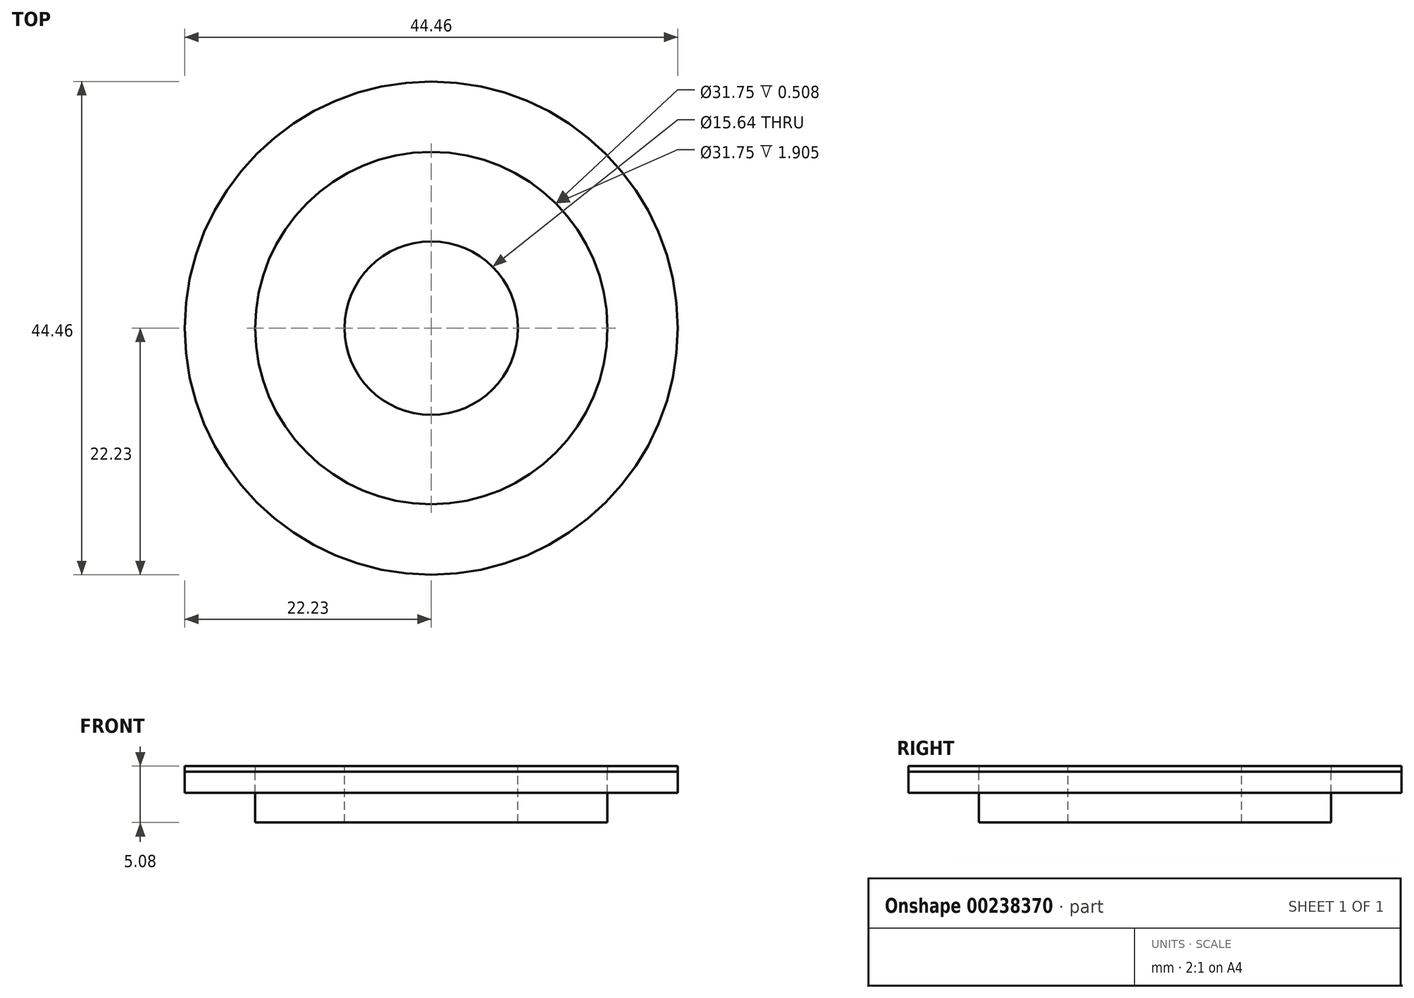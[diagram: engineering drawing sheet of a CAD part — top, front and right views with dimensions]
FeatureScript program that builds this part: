
annotation { "Feature Type Name" : "Feature", "Feature Type Description" : "" }
export const myFeature = defineFeature(function(context is Context, id is Id, definition is map)
    precondition{}
    {
        {
            var Q0;
            Q0=qCreatedBy(makeId("Top.planeOp"),FACE);
            var sketch = newSketch(context, id + "F0", { "sketchPlane" : qUnion([Q0])});
            skCircle(sketch, "E0", {"center": v(0, 0) * mm, "radius": 9.53 * mm});
            skCircle(sketch, "E1", {"center": v(0, 0) * mm, "radius": 22.23 * mm});
            skCircle(sketch, "E2", {"center": v(0, 0) * mm, "radius": 15.88 * mm});
            skSolve(sketch);
        }
        {
            var Q0;
            Q0=makeQuery(id+"F0.imprint","IMPRINT",FACE,{"disambiguationData":[TD([[makeQuery(id+"F0.imprint","IMPRINT",EDGE,{"derivedFrom":sQuery(id+"F0.wireOp",EDGE,"E1")}),1.0]])]});
            extrude(context, id + "F1", {"entities" : qUnion([Q0]), "oppositeDirection" : true, "depth" : 1.9 * mm});
        }
        {
            var Q0;
            Q0=makeQuery(id+"F1.opExtrude","CAP_FACE",FACE,{"disambiguationData":[OSD([sQuery(id+"F0.wireOp",EDGE,"E1"),sQuery(id+"F0.wireOp",EDGE,"E2")])],"isStart":true});
            extrude(context, id + "F2", {"entities" : qUnion([Q0]), "depth" : 0.5 * mm});
        }
        {
            var Q0;
            Q0=makeQuery(id+"F2.opExtrude","CAP_FACE",FACE,{"disambiguationData":[OSD([sQuery(id+"F0.wireOp",EDGE,"E1"),sQuery(id+"F0.wireOp",EDGE,"E2")])],"isStart":false});
            var sketch = newSketch(context, id + "F3", { "sketchPlane" : qUnion([Q0])});
            skCircle(sketch, "E3", {"center": v(0, 0) * mm, "radius": 7.82 * mm});
            skSolve(sketch);
        }
        {
            var Q0;
            Q0=makeQuery(id+"F3.imprint","IMPRINT",FACE,{"disambiguationData":[TD([[makeQuery(id+"F3.imprint","IMPRINT",EDGE,{"derivedFrom":sQuery(id+"F3.wireOp",EDGE,"E3")}),-1.0]])]});
            extrude(context, id + "F4", {"entities" : qUnion([Q0]), "oppositeDirection" : true, "depth" : 5.08 * mm});
        }
    });
